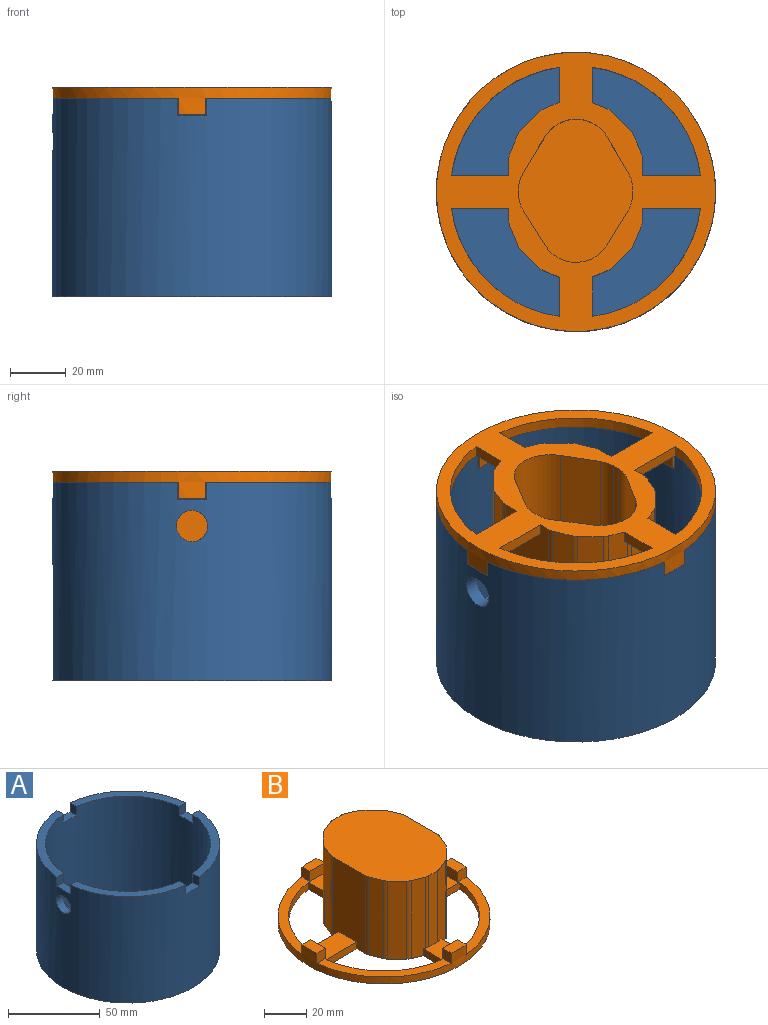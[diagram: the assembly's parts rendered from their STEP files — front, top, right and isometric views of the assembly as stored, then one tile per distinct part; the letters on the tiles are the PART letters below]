
ASSEMBLY  parts=2 mates=1
PART A: 23 faces, bbox 100x100x71 mm
  f0: cylinder r=50mm len=100mm, axis (0,0,-1), area 21961.4mm2, adj f1,f2,f4,f5,f6,f8,f9,f10
  f1: plane 44.64x44.64mm, normal (0,0,1), area 322mm2, adj f0,f3,f11,f19
  f2: plane 44.64x44.64mm, normal (0,0,1), area 322mm2, adj f0,f3,f9,f14
  f3: cylinder r=45mm len=90mm, axis (0,0,1), area 18033.9mm2, adj f1,f2,f4,f5,f7,f8,f9,f10
  f4: plane 44.64x44.64mm, normal (0,0,1), area 322mm2, adj f0,f3,f12,f15
  f5: plane 44.64x44.64mm, normal (0,0,1), area 322mm2, adj f0,f3,f8,f18
  f6: plane 100x100mm, normal (0,0,-1), area 7656.9mm2, adj f0,f21,f22
  f7: plane 90x90mm, normal (0,0,1), area 6164.7mm2, adj f3,f21,f22
  f8: plane 6x5.03mm, normal (-1,0,0), area 30.2mm2, adj f0,f3,f5,f10
  f9: plane 6x5.03mm, normal (1,0,0), area 30.2mm2, adj f0,f2,f3,f10
  f10: plane 10.2x5.29mm, normal (0,0,1), area 51.1mm2, adj f0,f3,f8,f9
  f11: plane 6x5.03mm, normal (-1,0,0), area 30.2mm2, adj f0,f1,f3,f13
  f12: plane 6x5.03mm, normal (1,0,0), area 30.2mm2, adj f0,f3,f4,f13
  f13: plane 10.2x5.29mm, normal (0,0,1), area 51.1mm2, adj f0,f3,f11,f12
  f14: plane 6x5.03mm, normal (0,-1,0), area 30.2mm2, adj f0,f2,f3,f16
  f15: plane 6x5.03mm, normal (0,1,0), area 30.2mm2, adj f0,f3,f4,f16
  f16: plane 10.2x5.29mm, normal (0,0,1), area 51.1mm2, adj f0,f3,f14,f15
  f17: plane 10.2x5.29mm, normal (0,0,1), area 51.1mm2, adj f0,f3,f18,f19
  f18: plane 6x5.03mm, normal (0,-1,0), area 30.2mm2, adj f0,f3,f5,f17
  f19: plane 6x5.03mm, normal (0,1,0), area 30.2mm2, adj f0,f1,f3,f17
  f20: cylinder r=5.6mm len=11.2mm, axis (1,0,0), area 176.5mm2, adj f0,f3
  f21: cylinder r=5.6mm len=11.2mm, axis (0,0,-1), area 211.1mm2, adj f6,f7
  f22: cylinder r=5.6mm len=11.2mm, axis (0,0,-1), area 211.1mm2, adj f6,f7
PART B: 77 faces, bbox 100x100x45 mm
  f0: plane 99.5x99.5mm, normal (0,0,1), area 2074.1mm2, adj f1,f2,f3,f4,f6,f7,f8,f9
  f1: plane 20.54x4mm, normal (0,1,0), area 82.1mm2, adj f0,f5,f6,f31
  f2: plane 20.54x4mm, normal (0,-1,0), area 82.1mm2, adj f0,f5,f7,f31
  f3: plane 12.59x4mm, normal (-1,0,0), area 50.4mm2, adj f0,f5,f7,f44
  f4: plane 12.71x4mm, normal (1,0,0), area 50.8mm2, adj f0,f5,f8,f43
  f5: plane 100x100mm, normal (0,0,-1), area 3362.4mm2, adj f1,f2,f3,f4,f6,f7,f8,f9
  f6: cylinder r=45mm len=38.6mm, axis (0,0,-1), area 234.6mm2, adj f0,f1,f5,f27
  f7: cylinder r=45mm len=38.6mm, axis (0,0,-1), area 234.6mm2, adj f0,f2,f3,f5
  f8: cylinder r=45mm len=38.6mm, axis (0,0,-1), area 234.6mm2, adj f0,f4,f5,f28
  f9: cylinder r=50mm len=100mm, axis (0,0,-1), area 1489mm2, adj f0,f5,f10,f12,f13,f15,f16,f17
  f10: plane 5.8x5.25mm, normal (-1,0,0), area 30.4mm2, adj f0,f9,f11,f13
  f11: plane 10x5.8mm, normal (0,-1,0), area 58mm2, adj f0,f10,f12,f13
  f12: plane 5.8x5.25mm, normal (1,0,0), area 30.4mm2, adj f0,f9,f11,f13
  f13: plane 10x5.5mm, normal (0,0,1), area 54.2mm2, adj f9,f10,f11,f12
  f14: plane 10x5.8mm, normal (0,1,0), area 58mm2, adj f0,f15,f16,f17
  f15: plane 5.8x5.75mm, normal (-1,0,0), area 33.3mm2, adj f0,f9,f14,f17
  f16: plane 5.8x5.75mm, normal (1,0,0), area 33.3mm2, adj f0,f9,f14,f17
  f17: plane 10x6mm, normal (0,0,1), area 59.2mm2, adj f9,f14,f15,f16
  f18: plane 5.8x5.75mm, normal (0,-1,0), area 33.3mm2, adj f0,f9,f19,f21
  f19: plane 10x5.8mm, normal (1,0,0), area 58mm2, adj f0,f18,f20,f21
  f20: plane 5.8x5.75mm, normal (0,1,0), area 33.3mm2, adj f0,f9,f19,f21
  f21: plane 10x6mm, normal (0,0,1), area 59.2mm2, adj f9,f18,f19,f20
  f22: plane 5.8x5.75mm, normal (0,1,0), area 33.3mm2, adj f0,f9,f23,f25
  f23: plane 10x5.8mm, normal (-1,0,0), area 58mm2, adj f0,f22,f24,f25
  f24: plane 5.8x5.75mm, normal (0,-1,0), area 33.3mm2, adj f0,f9,f23,f25
  f25: plane 10x6mm, normal (0,0,1), area 59.2mm2, adj f9,f22,f23,f24
  f26: cylinder r=45mm len=38.6mm, axis (0,0,-1), area 234.6mm2, adj f0,f5,f29,f30
  f27: plane 14.05x4mm, normal (-1,0,0), area 56.2mm2, adj f0,f5,f6,f47
  f28: plane 20.83x4mm, normal (0,-1,0), area 83.3mm2, adj f0,f5,f8,f33
  f29: plane 20.83x4mm, normal (0,1,0), area 83.3mm2, adj f0,f5,f26,f33
  f30: plane 14.17x4mm, normal (1,0,0), area 56.7mm2, adj f0,f5,f26,f46
  f31: plane 45x22.18mm, normal (-1,0,0), area 950mm2, adj f0,f1,f2,f5,f35,f62,f63
  f32: plane 41x5.84mm, normal (0,-1,0), area 239.6mm2, adj f0,f35,f52,f53
  f33: plane 45x22.18mm, normal (1,0,0), area 950mm2, adj f0,f5,f28,f29,f35,f58,f59
  f34: plane 41x5.84mm, normal (0,1,0), area 239.6mm2, adj f0,f35,f48,f49
  f35: plane 64.17x47.83mm, normal (0,0,1), area 2547.6mm2, adj f31,f32,f33,f34,f36,f37,f38,f39
  f36: plane 45x6.52mm, normal (-0.71,-0.71,0), area 415.1mm2, adj f5,f35,f50,f51
  f37: plane 45x6.52mm, normal (0.71,-0.71,0), area 415.1mm2, adj f5,f35,f54,f55
  f38: plane 45x6.52mm, normal (0.71,0.71,0), area 415.1mm2, adj f5,f35,f56,f57
  f39: plane 45x6.52mm, normal (-0.71,0.71,0), area 415.1mm2, adj f5,f35,f60,f61
  f40: plane 45x6.7mm, normal (-0.92,0.38,0), area 326.2mm2, adj f5,f35,f60,f62
  f41: plane 45x6.7mm, normal (0.92,0.38,0), area 326.2mm2, adj f5,f35,f56,f58
  f42: plane 45x6.7mm, normal (0.92,-0.38,0), area 326.2mm2, adj f5,f35,f54,f59
  f43: plane 45x6.7mm, normal (0.38,-0.92,0), area 320.6mm2, adj f0,f4,f5,f35,f52,f55
  f44: plane 45x6.7mm, normal (-0.38,-0.92,0), area 321.8mm2, adj f0,f3,f5,f35,f50,f53
  f45: plane 45x6.7mm, normal (-0.92,-0.38,0), area 326.2mm2, adj f5,f35,f51,f63
  f46: plane 45x6.7mm, normal (0.38,0.92,0), area 320.6mm2, adj f0,f5,f30,f35,f48,f57
  f47: plane 45x6.7mm, normal (-0.38,0.92,0), area 321.8mm2, adj f0,f5,f27,f35,f49,f61
  f48: cylinder r=5mm len=41mm, axis (0,0,-1), area 80.5mm2, adj f0,f34,f35,f46
  f49: cylinder r=5mm len=41mm, axis (0,0,-1), area 80.5mm2, adj f0,f34,f35,f47
  f50: cylinder r=5mm len=45mm, axis (0,0,1), area 88.4mm2, adj f5,f35,f36,f44
  f51: cylinder r=5mm len=45mm, axis (0,0,-1), area 88.4mm2, adj f5,f35,f36,f45
  f52: cylinder r=5mm len=41mm, axis (0,0,-1), area 80.5mm2, adj f0,f32,f35,f43
  f53: cylinder r=5mm len=41mm, axis (0,0,-1), area 80.5mm2, adj f0,f32,f35,f44
  f54: cylinder r=5mm len=45mm, axis (0,0,-1), area 88.4mm2, adj f5,f35,f37,f42
  f55: cylinder r=5mm len=45mm, axis (0,0,-1), area 88.4mm2, adj f5,f35,f37,f43
  f56: cylinder r=5mm len=45mm, axis (0,0,1), area 88.4mm2, adj f5,f35,f38,f41
  f57: cylinder r=5mm len=45mm, axis (0,0,-1), area 88.4mm2, adj f5,f35,f38,f46
  f58: cylinder r=5mm len=45mm, axis (0,0,1), area 88.4mm2, adj f5,f33,f35,f41
  f59: cylinder r=5mm len=45mm, axis (0,0,1), area 88.4mm2, adj f5,f33,f35,f42
  f60: cylinder r=5mm len=45mm, axis (0,0,1), area 88.4mm2, adj f5,f35,f39,f40
  f61: cylinder r=5mm len=45mm, axis (0,0,1), area 88.4mm2, adj f5,f35,f39,f47
  f62: cylinder r=5mm len=45mm, axis (0,0,1), area 88.4mm2, adj f5,f31,f35,f40
  f63: cylinder r=5mm len=45mm, axis (0,0,1), area 88.4mm2, adj f5,f31,f35,f45
  f64: cylinder r=13mm len=43mm, axis (0,0,-1), area 1164.9mm2, adj f5,f65,f71,f72
  f65: plane 43x13.15mm, normal (0.86,0.52,0), area 660.3mm2, adj f5,f64,f72,f73
  f66: plane 43x2.69mm, normal (1,0,0), area 115.5mm2, adj f5,f72,f73,f74
  f67: plane 43x12.59mm, normal (0.85,-0.53,0), area 640.6mm2, adj f5,f68,f72,f74
  f68: cylinder r=13mm len=43mm, axis (0,0,-1), area 1141.3mm2, adj f5,f67,f69,f72
  f69: plane 43x12.32mm, normal (-0.85,-0.52,0), area 621.6mm2, adj f5,f68,f72,f75
  f70: plane 43x2.84mm, normal (-1,0,0), area 122mm2, adj f5,f72,f75,f76
  f71: plane 43x12.88mm, normal (-0.86,0.5,0), area 641.5mm2, adj f5,f64,f72,f76
  f72: plane 51.27x40.71mm, normal (0,0,-1), area 1490.9mm2, adj f64,f65,f66,f67,f68,f69,f70,f71
  f73: cylinder r=10mm len=43mm, axis (0,0,1), area 233.4mm2, adj f5,f65,f66,f72
  f74: cylinder r=10mm len=43mm, axis (0,0,-1), area 242.5mm2, adj f5,f66,f67,f72
  f75: cylinder r=10mm len=43mm, axis (0,0,-1), area 236.5mm2, adj f5,f69,f70,f72
  f76: cylinder r=10mm len=43mm, axis (0,0,1), area 227.4mm2, adj f5,f70,f71,f72
PLACE A t=(46.96,38.55,-17.91)mm
PLACE B rot(axis=(1,0,0),180deg) t=(46.96,38.55,57.09)mm
MATE slider B.f6 <-> A.f3  axis (0,0,-1) through (46.96,38.55,53.09)mm
